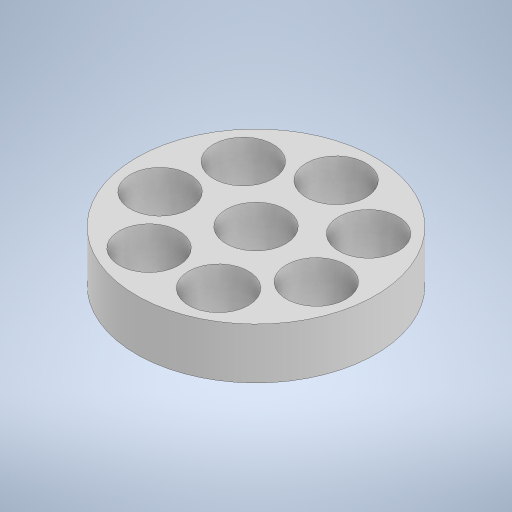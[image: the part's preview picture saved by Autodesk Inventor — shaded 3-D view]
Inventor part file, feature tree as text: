
AUTODESK INVENTOR PART (.ipt)
format: ipt  version: 2024 (Build 280153000, 153)  size: 260,608 bytes
history: native  units: mm
features: other x1, extrude x1, sketch x1
ambient origin geometry x8: Origin, YZ Plane, XZ Plane, XY Plane, X Axis, Y Axis, Z Axis, Center Point
bodies: Body1 (feature_tree)
feature tree (3):
  other  "솔리드1"
  extrude  "돌출1"  Depth=4.1mm
  sketch  "스케치1"
